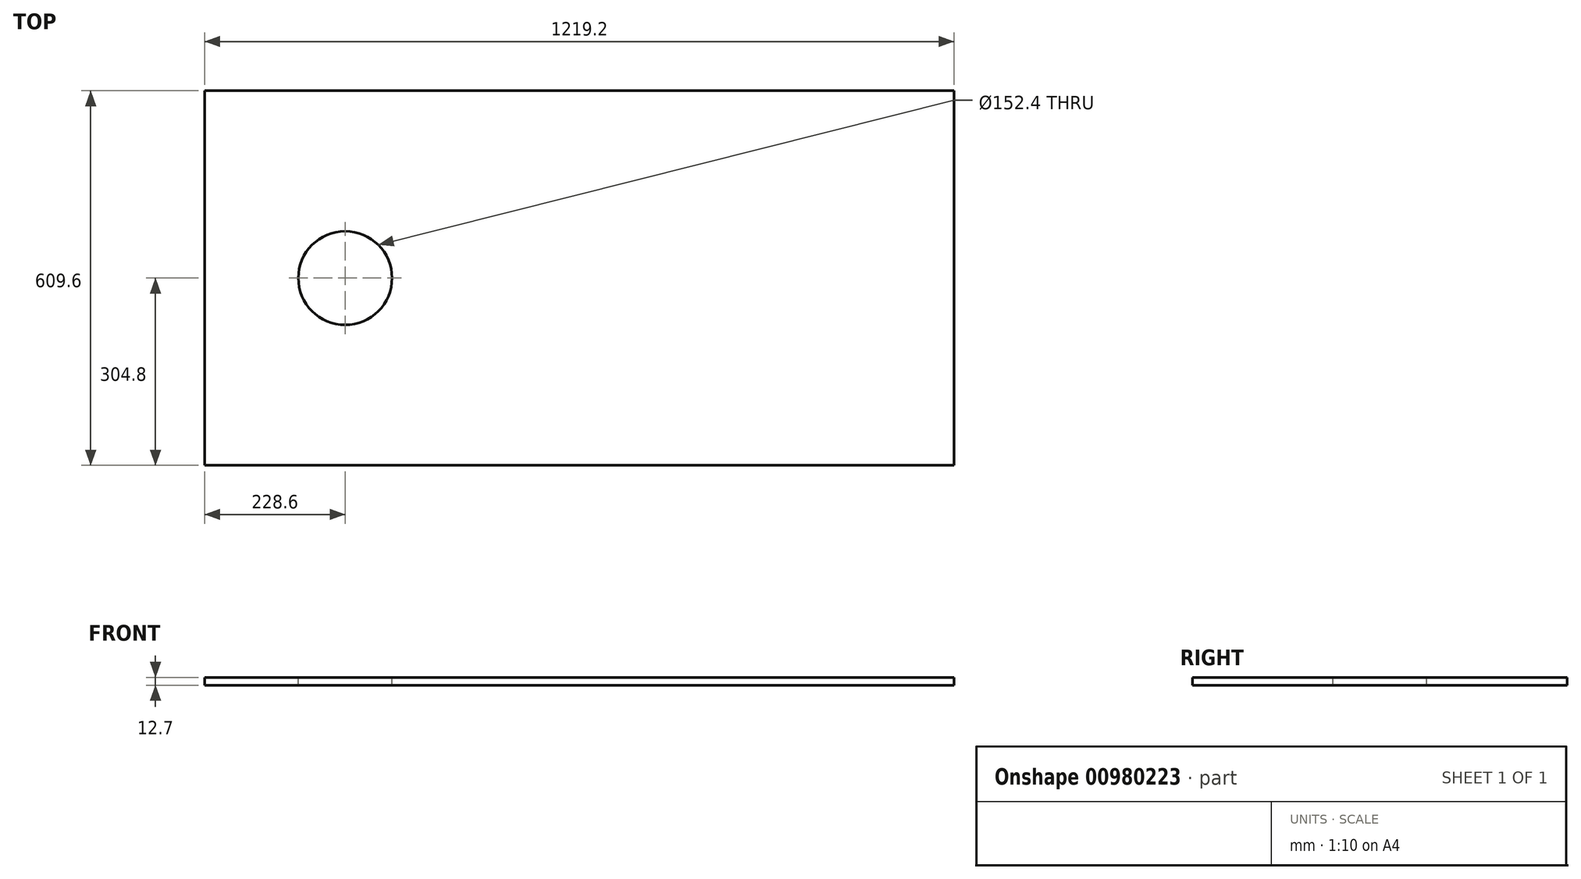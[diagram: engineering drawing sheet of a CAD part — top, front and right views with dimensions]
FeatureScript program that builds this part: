
annotation { "Feature Type Name" : "Feature", "Feature Type Description" : "" }
export const myFeature = defineFeature(function(context is Context, id is Id, definition is map)
    precondition{}
    {
        {
            var Q0;
            Q0=qCreatedBy(makeId("Top.planeOp"),FACE);
            var sketch = newSketch(context, id + "F0", { "sketchPlane" : qUnion([Q0])});
            skLineSegment(sketch, "E0.bottom", {"start": v(-609.6, 304.8) * mm, "end": v(609.6, 304.8) * mm});
            skLineSegment(sketch, "E0.top", {"start": v(-609.6, -304.8) * mm, "end": v(609.6, -304.8) * mm});
            skLineSegment(sketch, "E0.left", {"start": v(-609.6, 304.8) * mm, "end": v(-609.6, -304.8) * mm});
            skLineSegment(sketch, "E0.right", {"start": v(609.6, 304.8) * mm, "end": v(609.6, -304.8) * mm});
            skPoint(sketch, "E0.middle", {"position": v(0, 0) * mm});
            skSolve(sketch);
        }
        {
            var Q0;
            Q0 = qSketchRegion(id + "F0", true);
            extrude(context, id + "F1", {"entities" : qUnion([Q0]), "depth" : 12.7 * mm, "offsetDistance" : 25.4 * mm});
        }
        {
            var Q0;
            Q0=makeQuery(id+"F1.opExtrude","CAP_FACE",FACE,{"disambiguationData":[OSD([sQuery(id+"F0.wireOp",EDGE,"E0.bottom"),sQuery(id+"F0.wireOp",EDGE,"E0.top"),sQuery(id+"F0.wireOp",EDGE,"E0.left"),sQuery(id+"F0.wireOp",EDGE,"E0.right")])],"isStart":false});
            var sketch = newSketch(context, id + "F2", { "sketchPlane" : qUnion([Q0])});
            skLineSegment(sketch, "E1", {"start": v(-609.6, 0) * mm, "end": v(-381, 0) * mm, "construction": true});
            skSolve(sketch);
        }
        {
            var Q0;
            Q0=sQuery(id+"F2.wireOp",VERTEX,"E1.end");
            var Q1;
            Q1=makeQuery(id+"F1.opExtrude","SWEPT_BODY",BODY,{"disambiguationData":[OSD([sQuery(id+"F0.wireOp",EDGE,"E0.bottom"),sQuery(id+"F0.wireOp",EDGE,"E0.top"),sQuery(id+"F0.wireOp",EDGE,"E0.left"),sQuery(id+"F0.wireOp",EDGE,"E0.right")])]});
            hole(context, id + "F3", {"style" : HoleStyle.SIMPLE, "endStyle" : HoleEndStyle.THROUGH, "holeDiameter" : 152.4 * mm, "majorDiameter" : 6.35 * mm, "isTappedThrough" : true, "tappedDepth" : 12.7 * mm, "tapClearance" : 3, "locations" : qUnion([Q0]), "scope" : qUnion([Q1])});
        }
    });
